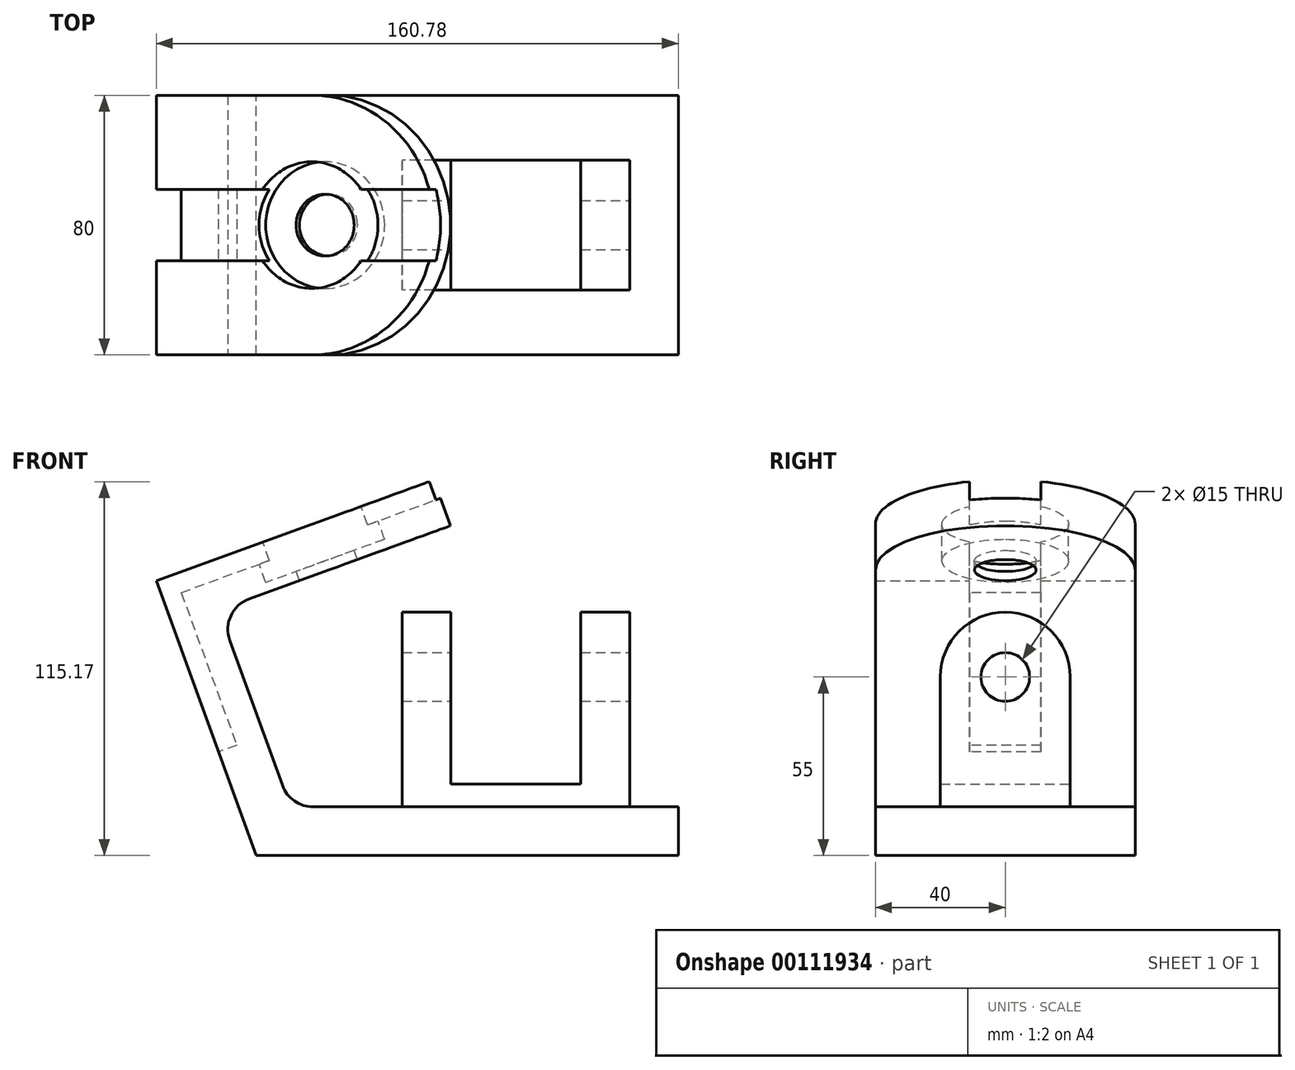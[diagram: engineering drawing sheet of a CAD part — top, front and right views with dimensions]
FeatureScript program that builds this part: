
annotation { "Feature Type Name" : "Feature", "Feature Type Description" : "" }
export const myFeature = defineFeature(function(context is Context, id is Id, definition is map)
    precondition{}
    {
        {
            var Q0;
            Q0=qCreatedBy(makeId("Front.planeOp"),FACE);
            var sketch = newSketch(context, id + "F0", { "sketchPlane" : qUnion([Q0])});
            skLineSegment(sketch, "E0", {"start": v(0, 0) * mm, "end": v(130, 0) * mm});
            skLineSegment(sketch, "E1", {"start": v(130, 0) * mm, "end": v(130, 15) * mm});
            skLineSegment(sketch, "E2", {"start": v(130, 15) * mm, "end": v(10.5, 15) * mm});
            skLineSegment(sketch, "E3", {"start": v(10.5, 15) * mm, "end": v(-11.56, 75.6) * mm});
            skLineSegment(sketch, "E4", {"start": v(-11.56, 75.6) * mm, "end": v(22.27, 87.92) * mm});
            skLineSegment(sketch, "E5", {"start": v(22.27, 87.92) * mm, "end": v(17.14, 102.02) * mm});
            skLineSegment(sketch, "E6", {"start": v(17.14, 102.02) * mm, "end": v(-30.78, 84.57) * mm});
            skLineSegment(sketch, "E7", {"start": v(-30.78, 84.57) * mm, "end": v(0, 0) * mm});
            skLineSegment(sketch, "E8", {"start": v(115, 15) * mm, "end": v(115, 55) * mm});
            skLineSegment(sketch, "E9", {"start": v(115, 55) * mm, "end": v(100, 55) * mm});
            skLineSegment(sketch, "E10", {"start": v(100, 55) * mm, "end": v(100, 22) * mm});
            skLineSegment(sketch, "E11", {"start": v(100, 22) * mm, "end": v(60, 22) * mm});
            skLineSegment(sketch, "E12", {"start": v(60, 22) * mm, "end": v(60, 55) * mm});
            skLineSegment(sketch, "E13", {"start": v(60, 55) * mm, "end": v(45, 55) * mm});
            skLineSegment(sketch, "E14", {"start": v(45, 55) * mm, "end": v(45, 15) * mm});
            skLineSegment(sketch, "E15", {"start": v(45, 15) * mm, "end": v(115, 15) * mm});
            skSolve(sketch);
        }
        {
            var Q0;
            Q0=makeQuery(id+"F0.imprint","IMPRINT",FACE,{"disambiguationData":[TD([[makeQuery(id+"F0.imprint","IMPRINT",EDGE,{"derivedFrom":sQuery(id+"F0.wireOp",EDGE,"E0")}),1.0]])]});
            extrude(context, id + "F1", {"entities" : qUnion([Q0]), "endBound" : BoundingType.SYMMETRIC, "depth" : 80 * mm});
        }
        {
            var Q0;
            Q0=makeQuery(id+"F1.opExtrude","SWEPT_FACE",FACE,{"disambiguationData":[OSD([sQuery(id+"F0.wireOp",EDGE,"E6")])]});
            var sketch = newSketch(context, id + "F2", { "sketchPlane" : qUnion([Q0])});
            skArc(sketch, "E16", {"start": v(51, -40) * mm, "mid": v(91, 0) * mm, "end": v(51, 40) * mm});
            skSolve(sketch);
        }
        {
            var Q0;
            Q0=makeQuery(id+"F2.imprint","IMPRINT",FACE,{"disambiguationData":[TD([[makeQuery(id+"F2.imprint","IMPRINT",EDGE,{"derivedFrom":sQuery(id+"F2.wireOp",EDGE,"E16")}),1.0]])]});
            extrude(context, id + "F3", {"entities" : qUnion([Q0]), "operationType" : NewBodyOperationType.ADD, "oppositeDirection" : true, "depth" : 15 * mm});
        }
        {
            var Q0;
            Q0 = qSketchRegion(id + "F0", true);
            extrude(context, id + "F4", {"entities" : qUnion([Q0]), "operationType" : NewBodyOperationType.ADD, "endBound" : BoundingType.SYMMETRIC, "depth" : 40 * mm});
        }
        {
            var Q0;
            Q0=makeQuery(id+"F4.opExtrude","SWEPT_FACE",FACE,{"disambiguationData":[OSD([sQuery(id+"F0.wireOp",EDGE,"E8")])]});
            var sketch = newSketch(context, id + "F5", { "sketchPlane" : qUnion([Q0])});
            skArc(sketch, "E17", {"start": v(20, 55) * mm, "mid": v(0, 75) * mm, "end": v(-20, 55) * mm});
            skSolve(sketch);
        }
        {
            var Q0;
            Q0=makeQuery(id+"F5.imprint","IMPRINT",FACE,{"disambiguationData":[TD([[makeQuery(id+"F5.imprint","IMPRINT",EDGE,{"derivedFrom":sQuery(id+"F5.wireOp",EDGE,"E17")}),1.0]])]});
            extrude(context, id + "F6", {"entities" : qUnion([Q0]), "operationType" : NewBodyOperationType.ADD, "oppositeDirection" : true, "depth" : 15 * mm});
        }
        {
            var Q0;
            Q0=makeQuery(id+"F4.opExtrude","SWEPT_FACE",FACE,{"disambiguationData":[OSD([sQuery(id+"F0.wireOp",EDGE,"E12")])]});
            var sketch = newSketch(context, id + "F7", { "sketchPlane" : qUnion([Q0])});
            skArc(sketch, "E18", {"start": v(20, 55) * mm, "mid": v(0, 75) * mm, "end": v(-20, 55) * mm});
            skSolve(sketch);
        }
        {
            var Q0;
            Q0 = qSketchRegion(id + "F7", true);
            var Q1;
            Q1=makeQuery(id+"F7.imprint","IMPRINT",FACE,{"disambiguationData":[TD([[makeQuery(id+"F7.imprint","IMPRINT",EDGE,{"derivedFrom":sQuery(id+"F7.wireOp",EDGE,"E18")}),1.0]])]});
            extrude(context, id + "F8", {"entities" : qUnion([Q0, Q1]), "operationType" : NewBodyOperationType.ADD, "oppositeDirection" : true, "depth" : 15 * mm});
        }
        {
            var Q0;
            {var subQ0=sQuery(id+"F0.wireOp",EDGE,"E8");Q0=makeQuery(id+"F6.boolean.opBoolean","MERGE",FACE,{"derivedFrom":[makeQuery(id+"F4.opExtrude","SWEPT_FACE",FACE,{"disambiguationData":[OSD([subQ0])]}),makeQuery(id+"F6.opExtrude","CAP_FACE",FACE,{"disambiguationData":[OSD([subQ0,sQuery(id+"F0.wireOp",EDGE,"E9"),sQuery(id+"F5.wireOp",EDGE,"E17")])],"isStart":true})]});}
            var sketch = newSketch(context, id + "F9", { "sketchPlane" : qUnion([Q0])});
            skCircle(sketch, "E19", {"center": v(0, 55) * mm, "radius": 7.5 * mm});
            skSolve(sketch);
        }
        {
            var Q0;
            Q0 = qSketchRegion(id + "F9", true);
            extrude(context, id + "F10", {"entities" : qUnion([Q0]), "operationType" : NewBodyOperationType.REMOVE, "oppositeDirection" : true, "depth" : 70 * mm});
        }
        {
            var Q0;
            Q0=makeQuery(id+"F1.opExtrude","SWEPT_FACE",FACE,{"disambiguationData":[OSD([sQuery(id+"F0.wireOp",EDGE,"E7")])]});
            var sketch = newSketch(context, id + "F11", { "sketchPlane" : qUnion([Q0])});
            skLineSegment(sketch, "E20.bottom", {"start": v(-11, 90) * mm, "end": v(11, 90) * mm});
            skLineSegment(sketch, "E20.top", {"start": v(-11, 34) * mm, "end": v(11, 34) * mm});
            skLineSegment(sketch, "E20.left", {"start": v(-11, 90) * mm, "end": v(-11, 34) * mm});
            skLineSegment(sketch, "E20.right", {"start": v(11, 90) * mm, "end": v(11, 34) * mm});
            skSolve(sketch);
        }
        {
            var Q0;
            {var subQ0=sQuery(id+"F0.wireOp",EDGE,"E6");Q0=makeQuery(id+"F3.boolean.opBoolean","MERGE",FACE,{"derivedFrom":[makeQuery(id+"F1.opExtrude","SWEPT_FACE",FACE,{"disambiguationData":[OSD([subQ0])]}),makeQuery(id+"F3.opExtrude","CAP_FACE",FACE,{"disambiguationData":[OSD([sQuery(id+"F0.wireOp",EDGE,"E5"),subQ0,sQuery(id+"F2.wireOp",EDGE,"E16")])],"isStart":true})]});}
            var sketch = newSketch(context, id + "F12", { "sketchPlane" : qUnion([Q0])});
            skLineSegment(sketch, "E21.bottom", {"start": v(0, 11) * mm, "end": v(95.2, 11) * mm});
            skLineSegment(sketch, "E21.top", {"start": v(0, -11) * mm, "end": v(95.2, -11) * mm});
            skLineSegment(sketch, "E21.left", {"start": v(0, 11) * mm, "end": v(0, -11) * mm});
            skLineSegment(sketch, "E21.right", {"start": v(95.2, 11) * mm, "end": v(95.2, -11) * mm});
            skSolve(sketch);
        }
        {
            var Q0;
            {var subQ0=sQuery(id+"F12.wireOp",EDGE,"E21.left");Q0=makeQuery(id+"F12.imprint","IMPRINT",FACE,{"disambiguationData":[TD([[makeQuery(id+"F12.imprint","IMPRINT",EDGE,{"derivedFrom":subQ0}),-1.0]])]});}
            extrude(context, id + "F13", {"entities" : qUnion([Q0]), "operationType" : NewBodyOperationType.REMOVE, "oppositeDirection" : true, "depth" : 6 * mm});
        }
        {
            var Q0;
            Q0=makeQuery(id+"F11.imprint","IMPRINT",FACE,{"disambiguationData":[TD([[makeQuery(id+"F11.imprint","IMPRINT",EDGE,{"derivedFrom":sQuery(id+"F11.wireOp",EDGE,"E20.bottom")}),1.0]])]});
            extrude(context, id + "F14", {"entities" : qUnion([Q0]), "operationType" : NewBodyOperationType.REMOVE, "oppositeDirection" : true, "depth" : 6 * mm});
        }
        {
            var Q0;
            {var subQ1=sQuery(id+"F0.wireOp",EDGE,"E6");var subQ2=sQuery(id+"F0.wireOp",EDGE,"E5");var subQ3=sQuery(id+"F2.wireOp",EDGE,"E16");Q0=makeQuery(id+"F13.boolean.opBoolean","SPLIT",FACE,{"disambiguationData":[TD([makeQuery(id+"F13.opExtrude","SWEPT_FACE",FACE,{"disambiguationData":[OSD([sQuery(id+"F12.wireOp",EDGE,"E21.top")])]})])],"derivedFrom":makeQuery(id+"F3.boolean.opBoolean","MERGE",FACE,{"derivedFrom":[makeQuery(id+"F1.opExtrude","SWEPT_FACE",FACE,{"disambiguationData":[OSD([subQ1])]}),makeQuery(id+"F3.opExtrude","CAP_FACE",FACE,{"disambiguationData":[OSD([subQ2,subQ1,subQ3])],"isStart":true})]})});}
            var sketch = newSketch(context, id + "F15", { "sketchPlane" : qUnion([Q0])});
            skCircle(sketch, "E22", {"center": v(51, 0) * mm, "radius": 9.5 * mm});
            skCircle(sketch, "E23", {"center": v(51, 0) * mm, "radius": 19.5 * mm});
            skSolve(sketch);
        }
        {
            var Q0;
            Q0=makeQuery(id+"F15.imprint","IMPRINT",FACE,{"disambiguationData":[TD([[makeQuery(id+"F15.imprint","IMPRINT",EDGE,{"derivedFrom":sQuery(id+"F15.wireOp",EDGE,"E22")}),1.0]])]});
            extrude(context, id + "F16", {"entities" : qUnion([Q0]), "operationType" : NewBodyOperationType.REMOVE, "oppositeDirection" : true, "depth" : 30 * mm});
        }
        {
            var Q0;
            Q0 = qSketchRegion(id + "F15", true);
            extrude(context, id + "F17", {"entities" : qUnion([Q0]), "operationType" : NewBodyOperationType.REMOVE, "oppositeDirection" : true, "depth" : 12 * mm});
        }
        {
            var Q0;
            Q0=makeQuery(id+"F1.opExtrude","SWEPT_EDGE",EDGE,{"disambiguationData":[OSD([sQuery(id+"F0.wireOp",EDGE,"E3"),sQuery(id+"F0.wireOp",EDGE,"E4")])]});
            var Q1;
            Q1=makeQuery(id+"F1.opExtrude","SWEPT_EDGE",EDGE,{"disambiguationData":[OSD([sQuery(id+"F0.wireOp",EDGE,"E2"),sQuery(id+"F0.wireOp",EDGE,"E3")])]});
            fillet(context, id + "F18", {"entities" : qUnion([Q0, Q1]), "radius" : 10 * mm, "tangentPropagation" : true, "allowEdgeOverflow" : false});
        }
    });
